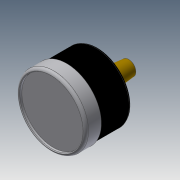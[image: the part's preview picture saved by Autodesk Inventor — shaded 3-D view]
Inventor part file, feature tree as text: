
AUTODESK INVENTOR PART (.ipt)
format: ipt  version: 2020.4 (Build 244396000, 396)  size: 2,854,400 bytes
history: native  units: in
note: dims shown in document units (in); Inventor stores cm internally (conversion verified against a paired STEP export)
features: imported_body x3, extrude x1, fillet x1, other x1
ambient origin geometry x8: Origin, YZ Plane, XZ Plane, XY Plane, X Axis, Y Axis, Z Axis, Center Point
bodies: Body1 (feature_tree), Body2 (feature_tree), Body3 (feature_tree)
feature tree (6):
  extrude  "Extrude10"  [1 undecoded]
  fillet  "Fillet2"  [1 undecoded]
  other  "Cut-Revolve1"
  imported_body  "Base1"
  imported_body  "Base2"
  imported_body  "Base3"
note: 2 required parameter values undecoded (feature->parameter linkage not recoverable at this tier; creation-order binding heuristic only, values carry confidence <= 0.55)
